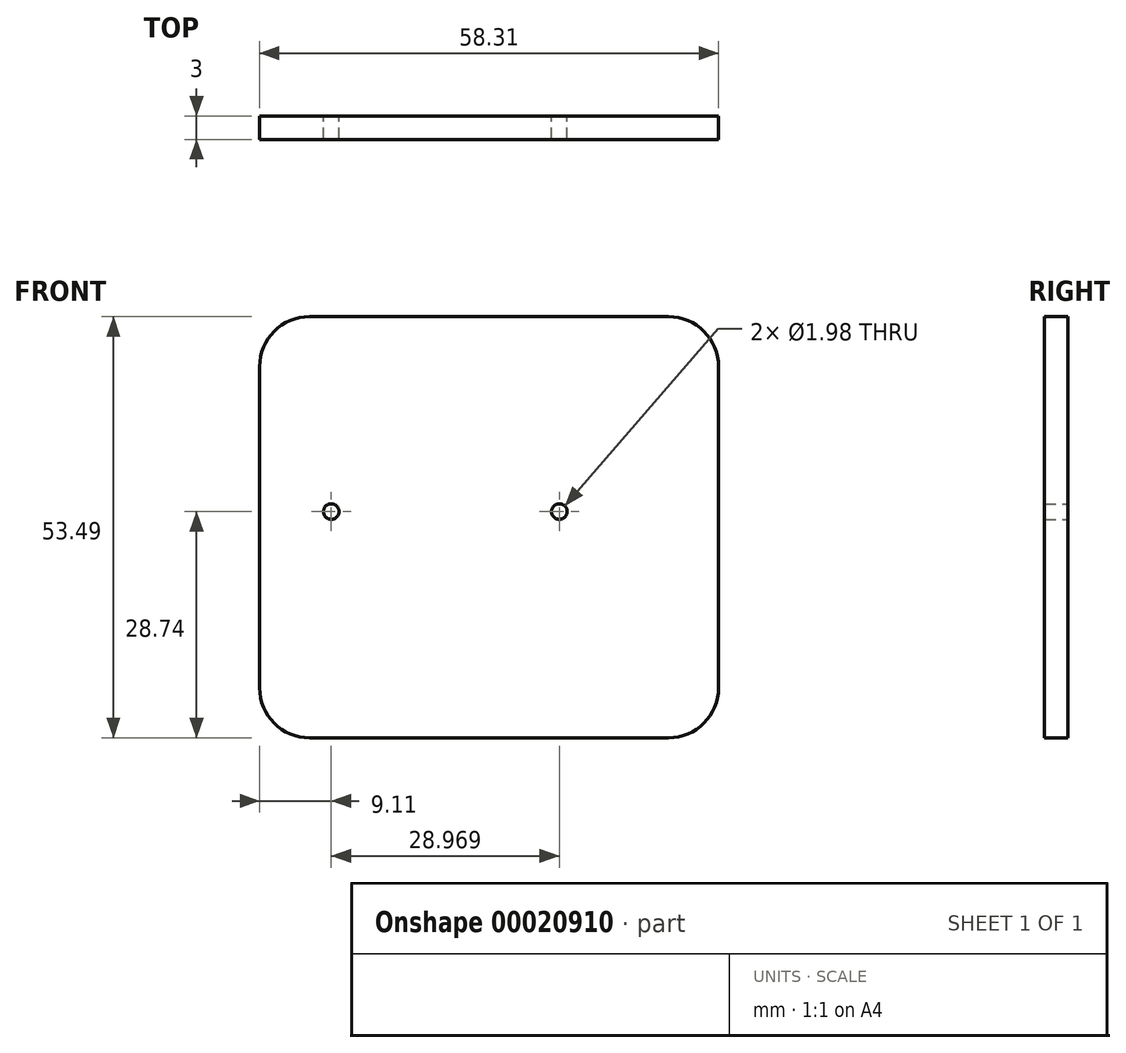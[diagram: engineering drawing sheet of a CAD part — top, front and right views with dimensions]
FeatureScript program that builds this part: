
annotation { "Feature Type Name" : "Feature", "Feature Type Description" : "" }
export const myFeature = defineFeature(function(context is Context, id is Id, definition is map)
    precondition{}
    {
        {
            var Q0;
            Q0=qCreatedBy(makeId("Front.planeOp"),FACE);
            var sketch = newSketch(context, id + "F0", { "sketchPlane" : qUnion([Q0])});
            skLineSegment(sketch, "E0.bottom", {"start": v(-2.76, 24.75) * mm, "end": v(42.85, 24.75) * mm});
            skLineSegment(sketch, "E0.top", {"start": v(-2.76, -28.74) * mm, "end": v(42.85, -28.74) * mm});
            skLineSegment(sketch, "E0.left", {"start": v(-9.1, 18.4) * mm, "end": v(-9.1, -22.39) * mm});
            skLineSegment(sketch, "E0.right", {"start": v(49.2, 18.4) * mm, "end": v(49.2, -22.39) * mm});
            skCircle(sketch, "E1", {"center": v(0, 0) * mm, "radius": 1 * mm});
            skCircle(sketch, "E2", {"center": v(28.97, 0) * mm, "radius": 1 * mm});
            skPoint(sketch, "E3.visualSharp", {"position": v(-9.1, 24.75) * mm});
            skArc(sketch, "E3.filletArc", {"start": v(-2.76, 24.75) * mm, "mid": v(-7.25, 22.9) * mm, "end": v(-9.1, 18.4) * mm});
            skPoint(sketch, "E4.visualSharp", {"position": v(49.2, 24.75) * mm});
            skArc(sketch, "E4.filletArc", {"start": v(49.2, 18.4) * mm, "mid": v(47.34, 22.9) * mm, "end": v(42.85, 24.75) * mm});
            skPoint(sketch, "E5.visualSharp", {"position": v(49.2, -28.74) * mm});
            skArc(sketch, "E5.filletArc", {"start": v(42.85, -28.74) * mm, "mid": v(47.34, -26.88) * mm, "end": v(49.2, -22.39) * mm});
            skPoint(sketch, "E6.visualSharp", {"position": v(-9.1, -28.74) * mm});
            skArc(sketch, "E6.filletArc", {"start": v(-9.1, -22.39) * mm, "mid": v(-7.25, -26.88) * mm, "end": v(-2.76, -28.74) * mm});
            skSolve(sketch);
        }
        {
            var Q0;
            Q0=makeQuery(id+"F0.imprint","IMPRINT",FACE,{"disambiguationData":[TD([[makeQuery(id+"F0.imprint","IMPRINT",EDGE,{"derivedFrom":sQuery(id+"F0.wireOp",EDGE,"E0.bottom")}),-1.0]])]});
            extrude(context, id + "F1", {"entities" : qUnion([Q0]), "depth" : 3 * mm});
        }
    });
